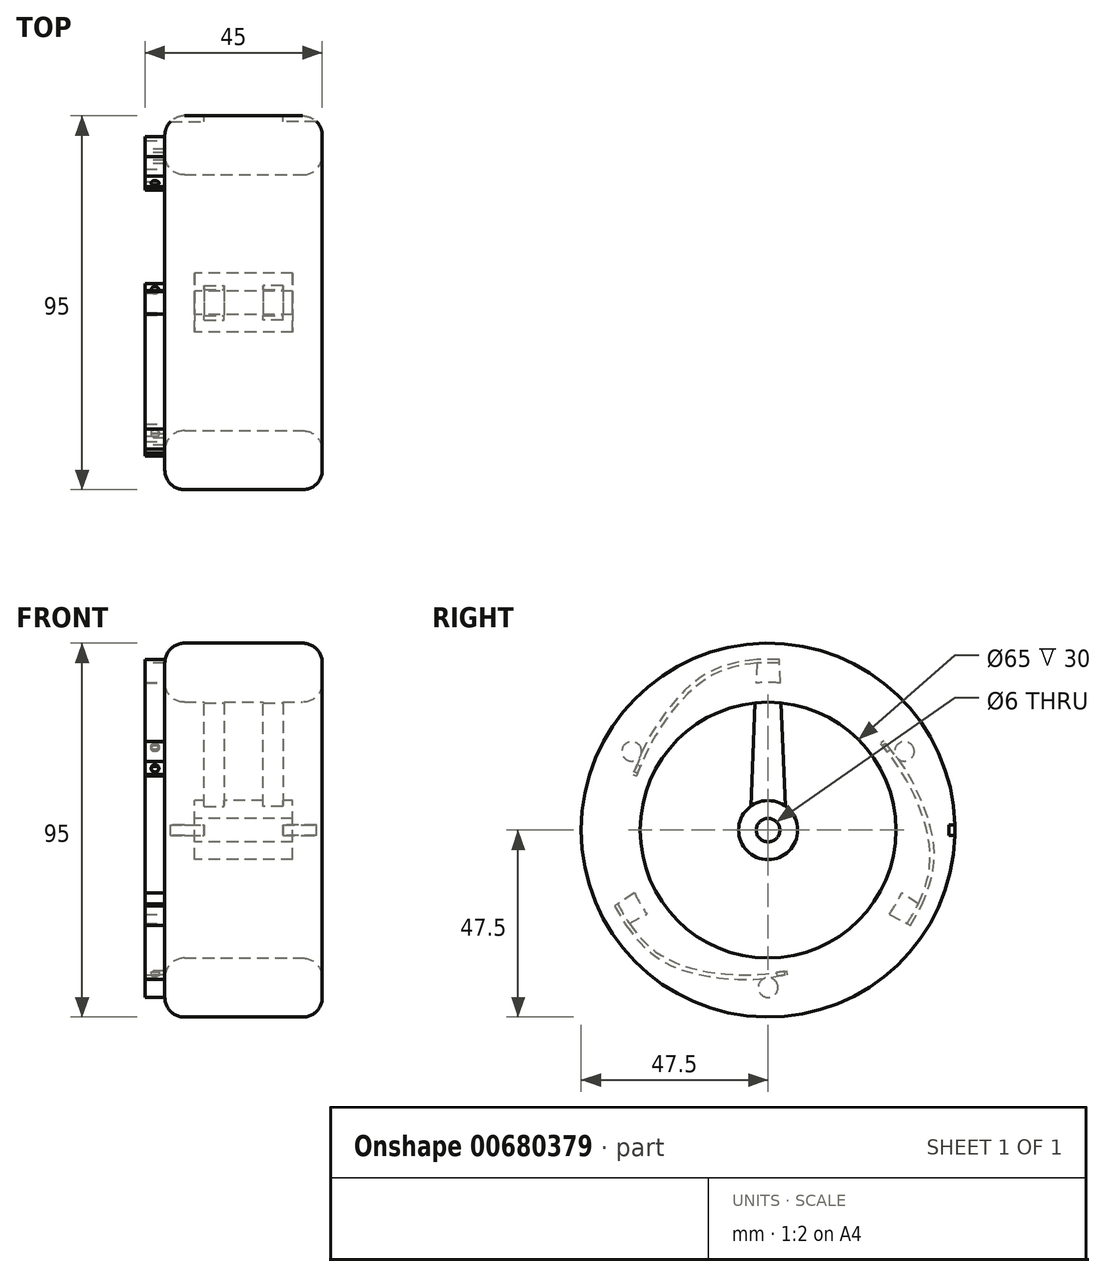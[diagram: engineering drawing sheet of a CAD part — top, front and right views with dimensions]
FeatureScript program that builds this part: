
annotation { "Feature Type Name" : "Feature", "Feature Type Description" : "" }
export const myFeature = defineFeature(function(context is Context, id is Id, definition is map)
    precondition{}
    {
        {
            var Q0;
            Q0=qCreatedBy(makeId("Right.planeOp"),FACE);
            var sketch = newSketch(context, id + "F0", { "sketchPlane" : qUnion([Q0])});
            skCircle(sketch, "E0", {"center": v(0, 0) * mm, "radius": 40 * mm});
            skPoint(sketch, "E1", {"position": v(0, 40) * mm});
            skPoint(sketch, "E2", {"position": v(0, -40) * mm});
            skSolve(sketch);
        }
        {
            var Q0;
            Q0=qCreatedBy(makeId("Front.planeOp"),FACE);
            var sketch = newSketch(context, id + "F1", { "sketchPlane" : qUnion([Q0])});
            skLineSegment(sketch, "E3.bottom", {"start": v(-15, 47.5) * mm, "end": v(15, 47.5) * mm});
            skLineSegment(sketch, "E3.top", {"start": v(-15, 32.5) * mm, "end": v(15, 32.5) * mm});
            skLineSegment(sketch, "E3.left", {"start": v(-20, 42.5) * mm, "end": v(-20, 37.5) * mm});
            skLineSegment(sketch, "E3.right", {"start": v(20, 42.5) * mm, "end": v(20, 37.5) * mm});
            skPoint(sketch, "E3.middle", {"position": v(0, 40) * mm});
            skPoint(sketch, "E4.visualSharp", {"position": v(-20, 47.5) * mm});
            skArc(sketch, "E4.filletArc", {"start": v(-15, 47.5) * mm, "mid": v(-18.54, 46.04) * mm, "end": v(-20, 42.5) * mm});
            skPoint(sketch, "E5.visualSharp", {"position": v(20, 32.5) * mm});
            skArc(sketch, "E5.filletArc", {"start": v(15, 32.5) * mm, "mid": v(18.54, 33.96) * mm, "end": v(20, 37.5) * mm});
            skPoint(sketch, "E6.visualSharp", {"position": v(-20, 32.5) * mm});
            skArc(sketch, "E6.filletArc", {"start": v(-20, 37.5) * mm, "mid": v(-18.54, 33.96) * mm, "end": v(-15, 32.5) * mm});
            skPoint(sketch, "E7.visualSharp", {"position": v(20, 47.5) * mm});
            skArc(sketch, "E7.filletArc", {"start": v(20, 42.5) * mm, "mid": v(18.54, 46.04) * mm, "end": v(15, 47.5) * mm});
            skLineSegment(sketch, "E8", {"start": v(44.27, 0) * mm, "end": v(-53.42, 0) * mm, "construction": true});
            skSolve(sketch);
        }
        {
            var Q0;
            Q0=qSketchRegion(id+"F1",true);
            var Q1;
            Q1=sQuery(id+"F0.wireOp",EDGE,"E0");
            sweep(context, id + "F2", {"profiles" : qUnion([Q0]), "path" : qUnion([Q1])});
        }
        {
            var Q0;
            Q0=qCreatedBy(makeId("Right.planeOp"),FACE);
            var sketch = newSketch(context, id + "F3", { "sketchPlane" : qUnion([Q0])});
            skLineSegment(sketch, "E9.bottom", {"start": v(46, 1.35) * mm, "end": v(49, 1.35) * mm});
            skLineSegment(sketch, "E9.top", {"start": v(46, -1.35) * mm, "end": v(49, -1.35) * mm});
            skLineSegment(sketch, "E9.left", {"start": v(46, 1.35) * mm, "end": v(46, -1.35) * mm});
            skLineSegment(sketch, "E9.right", {"start": v(49, 1.35) * mm, "end": v(49, -1.35) * mm});
            skPoint(sketch, "E9.middle", {"position": v(47.5, 0) * mm});
            skSolve(sketch);
        }
        {
            var Q0;
            Q0=makeQuery(id+"F3.imprint","IMPRINT",FACE,{"disambiguationData":[TD([[makeQuery(id+"F3.imprint","IMPRINT",EDGE,{"derivedFrom":sQuery(id+"F3.wireOp",EDGE,"E9.bottom")}),-1.0]])]});
            extrude(context, id + "F4", {"entities" : qUnion([Q0]), "operationType" : NewBodyOperationType.REMOVE, "oppositeDirection" : true, "depth" : 20 * mm, "offsetDistance" : 25 * mm, "hasSecondDirection" : true, "secondDirectionOppositeDirection" : true, "secondDirectionDepth" : 10 * mm});
        }
        {
            var Q0;
            Q0=makeQuery(id+"F3.imprint","IMPRINT",FACE,{"disambiguationData":[TD([[makeQuery(id+"F3.imprint","IMPRINT",EDGE,{"derivedFrom":sQuery(id+"F3.wireOp",EDGE,"E9.bottom")}),-1.0]])]});
            extrude(context, id + "F5", {"entities" : qUnion([Q0]), "operationType" : NewBodyOperationType.REMOVE, "depth" : 20 * mm, "offsetDistance" : 25 * mm, "hasSecondDirection" : true, "secondDirectionOppositeDirection" : true, "secondDirectionDepth" : -10 * mm});
        }
        {
            var Q0;
            Q0=qCreatedBy(makeId("Right.planeOp"),FACE);
            var sketch = newSketch(context, id + "F6", { "sketchPlane" : qUnion([Q0])});
            skCircle(sketch, "E10", {"center": v(0, 0) * mm, "radius": 7.5 * mm});
            skLineSegment(sketch, "E11", {"start": v(0, 0) * mm, "end": v(0, 37.37) * mm, "construction": true});
            skLineSegment(sketch, "E12", {"start": v(0, 0) * mm, "end": v(30.9, 10.04) * mm, "construction": true});
            skLineSegment(sketch, "E13", {"start": v(0, 0) * mm, "end": v(19.1, -26.3) * mm, "construction": true});
            skLineSegment(sketch, "E14", {"start": v(0, 0) * mm, "end": v(-19.1, -26.3) * mm, "construction": true});
            skLineSegment(sketch, "E15", {"start": v(0, 0) * mm, "end": v(-30.9, 10.04) * mm, "construction": true});
            skLineSegment(sketch, "E16", {"start": v(0, 0) * mm, "end": v(-19.1, 26.3) * mm, "construction": true});
            skLineSegment(sketch, "E17", {"start": v(0, 0) * mm, "end": v(19.1, 26.3) * mm, "construction": true});
            skLineSegment(sketch, "E18", {"start": v(-4.4, 6.07) * mm, "end": v(-3.1, 37.37) * mm});
            skLineSegment(sketch, "E19", {"start": v(-3.1, 37.37) * mm, "end": v(3.1, 37.37) * mm});
            skLineSegment(sketch, "E20", {"start": v(3.1, 37.37) * mm, "end": v(4.4, 6.07) * mm});
            skCircle(sketch, "E21", {"center": v(0, 0) * mm, "radius": 3 * mm});
            skSolve(sketch);
        }
        {
            var Q0;
            {var subQ0=sQuery(id+"F6.wireOp",EDGE,"E18");Q0=makeQuery(id+"F6.imprint","IMPRINT",FACE,{"disambiguationData":[TD([[makeQuery(id+"F6.imprint","IMPRINT",EDGE,{"derivedFrom":subQ0}),-1.0]])]});}
            extrude(context, id + "F7", {"entities" : qUnion([Q0]), "operationType" : NewBodyOperationType.ADD, "depth" : 10 * mm, "offsetDistance" : 25 * mm, "hasSecondDirection" : true, "secondDirectionOppositeDirection" : false, "secondDirectionDepth" : 5 * mm});
        }
        {
            var Q0;
            {var subQ0=sQuery(id+"F6.wireOp",EDGE,"E18");Q0=makeQuery(id+"F6.imprint","IMPRINT",FACE,{"disambiguationData":[TD([[makeQuery(id+"F6.imprint","IMPRINT",EDGE,{"derivedFrom":subQ0}),-1.0]])]});}
            extrude(context, id + "F8", {"entities" : qUnion([Q0]), "operationType" : NewBodyOperationType.ADD, "oppositeDirection" : true, "depth" : 10 * mm, "offsetDistance" : 25 * mm, "hasSecondDirection" : true, "secondDirectionOppositeDirection" : true, "secondDirectionDepth" : 5 * mm});
        }
        {
            var Q0;
            Q0=makeQuery(id+"F6.imprint","IMPRINT",FACE,{"disambiguationData":[TD([[makeQuery(id+"F6.imprint","IMPRINT",EDGE,{"derivedFrom":sQuery(id+"F6.wireOp",EDGE,"E21")}),-1.0]])]});
            extrude(context, id + "F9", {"entities" : qUnion([Q0]), "operationType" : NewBodyOperationType.ADD, "depth" : 25 * mm, "offsetDistance" : 25 * mm, "symmetric" : true});
        }
        {
            var Q0;
            Q0=makeQuery(id+"F2.opSweep","SWEPT_FACE",FACE,{"disambiguationData":[OSD([sQuery(id+"F0.wireOp",EDGE,"E0"),sQuery(id+"F1.wireOp",EDGE,"E3.left")])]});
            var sketch = newSketch(context, id + "F10", { "sketchPlane" : qUnion([Q0])});
            skLineSegment(sketch, "E22", {"start": v(-3.1, 37.37) * mm, "end": v(-2.89, 42.4) * mm});
            skLineSegment(sketch, "E23", {"start": v(2.89, 42.4) * mm, "end": v(3.1, 37.37) * mm});
            skArc(sketch, "E24", {"start": v(-3.1, 37.37) * mm, "mid": v(0, 37.5) * mm, "end": v(3.1, 37.37) * mm});
            skArc(sketch, "E25", {"start": v(-2.89, 42.4) * mm, "mid": v(0, 42.5) * mm, "end": v(2.89, 42.4) * mm});
            skLineSegment(sketch, "E26", {"start": v(0, 0) * mm, "end": v(60.38, 34.86) * mm, "construction": true});
            skCircle(sketch, "E27", {"center": v(34.64, 20) * mm, "radius": 2.5 * mm});
            skPoint(sketch, "E28", {"position": v(32.48, 18.75) * mm});
            skSolve(sketch);
        }
        {
            var Q0;
            Q0=makeQuery(id+"F10.imprint","IMPRINT",FACE,{"disambiguationData":[TD([[makeQuery(id+"F10.imprint","IMPRINT",EDGE,{"derivedFrom":sQuery(id+"F10.wireOp",EDGE,"E22")}),-1.0]])]});
            var Q1;
            {var subQ0=sQuery(id+"F10.wireOp",EDGE,"E27");var subQ1=sQuery(id+"F1.wireOp",EDGE,"E3.left");var subQ2=sQuery(id+"F0.wireOp",EDGE,"E0");var subQ3=makeQuery(id+"F10.imprint","INTERSECT",VERTEX,{"derivedFrom":[makeQuery(id+"F2.opSweep","SWEPT_EDGE",EDGE,{"disambiguationData":[OSD([subQ2,subQ1,sQuery(id+"F1.wireOp",EDGE,"E4.filletArc")])]}),subQ0]});Q1=makeQuery(id+"F10.imprint","IMPRINT",FACE,{"disambiguationData":[TD([[makeQuery(id+"F10.imprint","IMPRINT",EDGE,{"disambiguationData":[TD([[subQ3,-1.0]])],"derivedFrom":subQ0}),1.0]])]});}
            extrude(context, id + "F11", {"entities" : qUnion([Q0, Q1]), "depth" : 5 * mm, "offsetDistance" : 25 * mm});
        }
        {
            var Q0;
            Q0=makeQuery(id+"F11.opExtrude","CAP_FACE",FACE,{"disambiguationData":[OSD([sQuery(id+"F10.wireOp",EDGE,"E22"),sQuery(id+"F10.wireOp",EDGE,"E23"),sQuery(id+"F10.wireOp",EDGE,"E24"),sQuery(id+"F10.wireOp",EDGE,"E25")])],"isStart":false});
            var sketch = newSketch(context, id + "F12", { "sketchPlane" : qUnion([Q0])});
            skLineSegment(sketch, "E29", {"start": v(-2.89, 42.4) * mm, "end": v(-2.85, 43.4) * mm});
            skLineSegment(sketch, "E30", {"start": v(-2.85, 43.4) * mm, "end": v(2.85, 43.4) * mm});
            skLineSegment(sketch, "E31", {"start": v(2.85, 43.4) * mm, "end": v(2.89, 42.4) * mm});
            skLineSegment(sketch, "E32", {"start": v(34.33, 14.18) * mm, "end": v(33.43, 13.74) * mm});
            skFitSpline(sketch, "E33", {"points": [v(2.85, 43.4) * mm, v(11.34, 41.68) * mm, v(20.72, 35.91) * mm, v(29.82, 24.26) * mm, v(32.48, 18.75) * mm, v(34.33, 14.18) * mm], "startDerivative": vector(42.92, -5.79) * mm, "endDerivative": vector(14.89, -30.27) * mm});
            skFitSpline(sketch, "E34", {"points": [v(2.89, 42.4) * mm, v(10.68, 40.9) * mm, v(19.92, 35.11) * mm, v(28.87, 23.54) * mm, v(33.43, 13.74) * mm], "startDerivative": vector(36.33, -4.15) * mm, "endDerivative": vector(15.62, -38.41) * mm});
            skSolve(sketch);
        }
        {
            var Q0;
            Q0=makeQuery(id+"F12.imprint","IMPRINT",FACE,{"disambiguationData":[TD([[makeQuery(id+"F12.imprint","IMPRINT",EDGE,{"derivedFrom":sQuery(id+"F12.wireOp",EDGE,"E31")}),1.0]])]});
            var Q1;
            Q1=makeQuery(id+"F12.imprint","IMPRINT",FACE,{"disambiguationData":[TD([[makeQuery(id+"F12.imprint","IMPRINT",EDGE,{"derivedFrom":sQuery(id+"F12.wireOp",EDGE,"E29")}),-1.0]])]});
            extrude(context, id + "F13", {"entities" : qUnion([Q0, Q1]), "oppositeDirection" : true, "depth" : 5 * mm, "offsetDistance" : 25 * mm});
        }
        {
            var Q0;
            Q0=makeQuery(id+"F13.opExtrude","SWEPT_FACE",FACE,{"disambiguationData":[OSD([sQuery(id+"F12.wireOp",EDGE,"E32")])]});
            var sketch = newSketch(context, id + "F14", { "sketchPlane" : qUnion([Q0])});
            skLineSegment(sketch, "E35", {"start": v(-22.5, 36.05) * mm, "end": v(-22.5, 38.01) * mm, "construction": true});
            skSolve(sketch);
        }
        {
            var Q0;
            Q0=makeQuery(id+"F11.opExtrude","SWEPT_EDGE",EDGE,{"disambiguationData":[OSD([sQuery(id+"F0.wireOp",EDGE,"E0"),sQuery(id+"F1.wireOp",EDGE,"E3.left"),sQuery(id+"F1.wireOp",EDGE,"E6.filletArc"),sQuery(id+"F10.wireOp",EDGE,"E23"),sQuery(id+"F10.wireOp",EDGE,"E24")])]});
            cPoint(context, id + "F15", {"entities" : qUnion([Q0]), "parameter" : 0.5});
        }
        {
            var Q0;
            Q0=sQuery(id+"F14.wireOp",VERTEX,"E35.end");
            var Q1;
            Q1=sQuery(id+"F14.wireOp",VERTEX,"E35.start");
            var Q2;
            Q2 = qCreatedBy(id + "F15" ,VERTEX);
            cPlane(context, id + "F16", {"entities" : qUnion([Q0, Q1, Q2]), "cplaneType" : CPlaneType.THREE_POINT, "offset" : 25 * mm, "width" : 150 * mm, "height" : 150 * mm});
        }
        {
            var Q0;
            Q0=qCreatedBy(id+"F16.planeOp",FACE);
            var sketch = newSketch(context, id + "F17", { "sketchPlane" : qUnion([Q0])});
            skLineSegment(sketch, "E36", {"start": v(27.83, 12.83) * mm, "end": v(41.02, 19.42) * mm});
            skLineSegment(sketch, "E37", {"start": v(29.1, 13.47) * mm, "end": v(29.56, 12.57) * mm});
            skLineSegment(sketch, "E38", {"start": v(29.56, 12.57) * mm, "end": v(35.84, 15.71) * mm});
            skLineSegment(sketch, "E39", {"start": v(35.84, 15.71) * mm, "end": v(35.39, 16.6) * mm});
            skSolve(sketch);
        }
        {
            var Q0;
            {var subQ0=sQuery(id+"F17.wireOp",EDGE,"E37");Q0=makeQuery(id+"F17.imprint","IMPRINT",FACE,{"disambiguationData":[TD([[makeQuery(id+"F17.imprint","IMPRINT",EDGE,{"derivedFrom":subQ0}),1.0]])]});}
            var Q1;
            Q1=sQuery(id+"F17.wireOp",EDGE,"E36");
            revolve(context, id + "F18", {"operationType" : NewBodyOperationType.REMOVE, "entities" : qUnion([Q0]), "axis" : qUnion([Q1]), "revolveType" : RevolveType.FULL, "oppositeDirection" : true});
        }
        {
            var Q0;
            Q0=makeQuery(id+"F11.opExtrude","SWEPT_BODY",BODY,{"disambiguationData":[OSD([sQuery(id+"F10.wireOp",EDGE,"E22"),sQuery(id+"F10.wireOp",EDGE,"E23"),sQuery(id+"F10.wireOp",EDGE,"E24"),sQuery(id+"F10.wireOp",EDGE,"E25")])]});
            var Q1;
            Q1=makeQuery(id+"F13.opExtrude","SWEPT_BODY",BODY,{"disambiguationData":[OSD([sQuery(id+"F10.wireOp",EDGE,"E25"),sQuery(id+"F12.wireOp",EDGE,"E29"),sQuery(id+"F12.wireOp",EDGE,"E30"),sQuery(id+"F12.wireOp",EDGE,"E32"),sQuery(id+"F12.wireOp",EDGE,"E33"),sQuery(id+"F12.wireOp",EDGE,"E34")])]});
            var Q2;
            Q2=makeQuery(id+"F11.opExtrude","SWEPT_BODY",BODY,{"disambiguationData":[OSD([sQuery(id+"F10.wireOp",EDGE,"E27")])]});
            var Q3;
            Q3=makeQuery(id+"F9.opExtrude","CAP_EDGE",EDGE,{"disambiguationData":[OSD([sQuery(id+"F6.wireOp",EDGE,"E21")])],"isStart":true});
            circularPattern(context, id + "F19", {"entities" : qUnion([Q0, Q1, Q2]), "axis" : qUnion([Q3]), "angle" : 360 * degree, "instanceCount" : 3, "equalSpace" : true});
        }
    });
